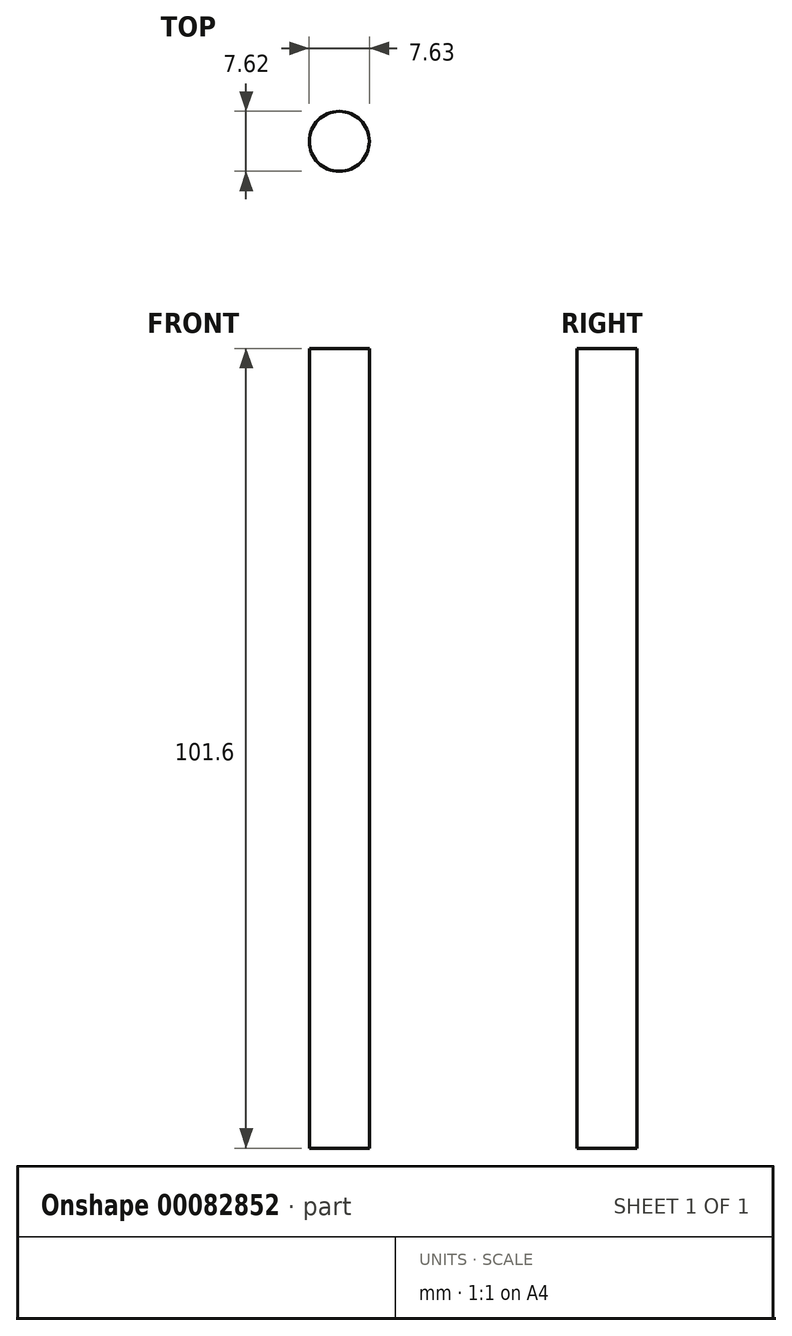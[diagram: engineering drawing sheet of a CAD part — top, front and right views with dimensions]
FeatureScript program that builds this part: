
annotation { "Feature Type Name" : "Feature", "Feature Type Description" : "" }
export const myFeature = defineFeature(function(context is Context, id is Id, definition is map)
    precondition{}
    {
        {
            var Q0;
            Q0=qCreatedBy(makeId("Front.planeOp"),FACE);
            var sketch = newSketch(context, id + "F0", { "sketchPlane" : qUnion([Q0])});
            skLineSegment(sketch, "E0.bottom", {"start": v(-1.9, 50.8) * mm, "end": v(1.9, 50.8) * mm});
            skLineSegment(sketch, "E0.top", {"start": v(-1.9, -50.8) * mm, "end": v(1.9, -50.8) * mm});
            skLineSegment(sketch, "E0.left", {"start": v(-1.9, 50.8) * mm, "end": v(-1.9, -50.8) * mm});
            skLineSegment(sketch, "E0.right", {"start": v(1.9, 50.8) * mm, "end": v(1.9, -50.8) * mm});
            skPoint(sketch, "E0.middle", {"position": v(0, 0) * mm});
            skSolve(sketch);
        }
        {
            var Q0;
            Q0=makeQuery(id+"F0.imprint","IMPRINT",FACE,{"disambiguationData":[TD([[makeQuery(id+"F0.imprint","IMPRINT",EDGE,{"derivedFrom":sQuery(id+"F0.wireOp",EDGE,"E0.bottom")}),-1.0]])]});
            var Q1;
            Q1=sQuery(id+"F0.wireOp",EDGE,"E0.right");
            revolve(context, id + "F1", {"entities" : qUnion([Q0]), "axis" : qUnion([Q1]), "revolveType" : RevolveType.FULL});
        }
    });
